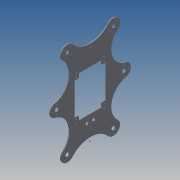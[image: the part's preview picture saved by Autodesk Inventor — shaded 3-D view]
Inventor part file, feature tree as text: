
AUTODESK INVENTOR PART (.ipt)
format: ipt  version: 2014 (Build 180170000, 170)  size: 289,792 bytes
history: native  units: mm
features: sketch x5, extrude x1
ambient origin geometry x8: Origin, YZ Plane, XZ Plane, XY Plane, X Axis, Y Axis, Z Axis, Center Point
bodies: Solid1 (feature_tree)
feature tree (6):
  sketch  "Sketch1"  dims[d0=165.0mm d1=85.5mm d2=82.5mm d3=20.0mm d4=20.0mm d5=25.0mm d6=25.0mm d7=25.0mm d8=25.0mm d9=25.0mm d10=25.0mm d11=7.0mm d12=7.0mm d13=7.0mm d14=7.0mm d15=7.0mm d16=7.0mm d17=45.0deg d18=45.0deg d19=45.0deg d20=45.0deg d21=45.0deg d22=45.0deg d23=45.0deg d24=90.0deg d27=11.0mm d28=11.0mm d29=150.680282mm d30=61.6967mm d43=2.0mm d44=6.5mm d46=2.0mm d49=17.0mm d51=2.0mm d52=2.0mm d55=17.0mm d56=17.0mm d57=2.0mm]
  sketch  "Sketch2"  dims[d58=2.0mm]
  sketch  "Sketch3"  dims[d59=8.0mm]
  sketch  "Sketch4"  dims[d61=2.0mm]
  sketch  "Sketch5"  dims[d62=8.0mm d63=2.0mm d64=8.0mm d67=42.0mm d70=58.0mm d71=76.0mm d72=2.0mm d76=12.5mm d78=36.5mm d79=90.0deg d80=90.0deg d81=90.0deg d82=90.0deg d88=1.5mm d89=1.5mm d90=1.5mm d91=1.5mm d92=1.5mm d93=1.5mm d94=1.5mm d95=1.5mm d96=3.999mm d97=3.999mm d98=3.999mm d99=3.999mm d104=3.998972mm d105=3.998972mm d106=3.999mm d107=3.999mm d109=1.5mm d110=1.5mm d111=1.5mm d112=1.5mm d113=3.999mm d114=1.5mm d115=1.5mm d116=1.5mm d117=1.5mm d118=3.999mm d119=1.5mm d120=1.5mm d121=1.5mm d122=1.5mm d123=7.0mm d124=1.5mm d125=1.5mm d126=1.5mm d127=1.5mm d128=1.5mm d129=0.0mm]
  extrude  "Extrusion1"  Depth=2.0mm
